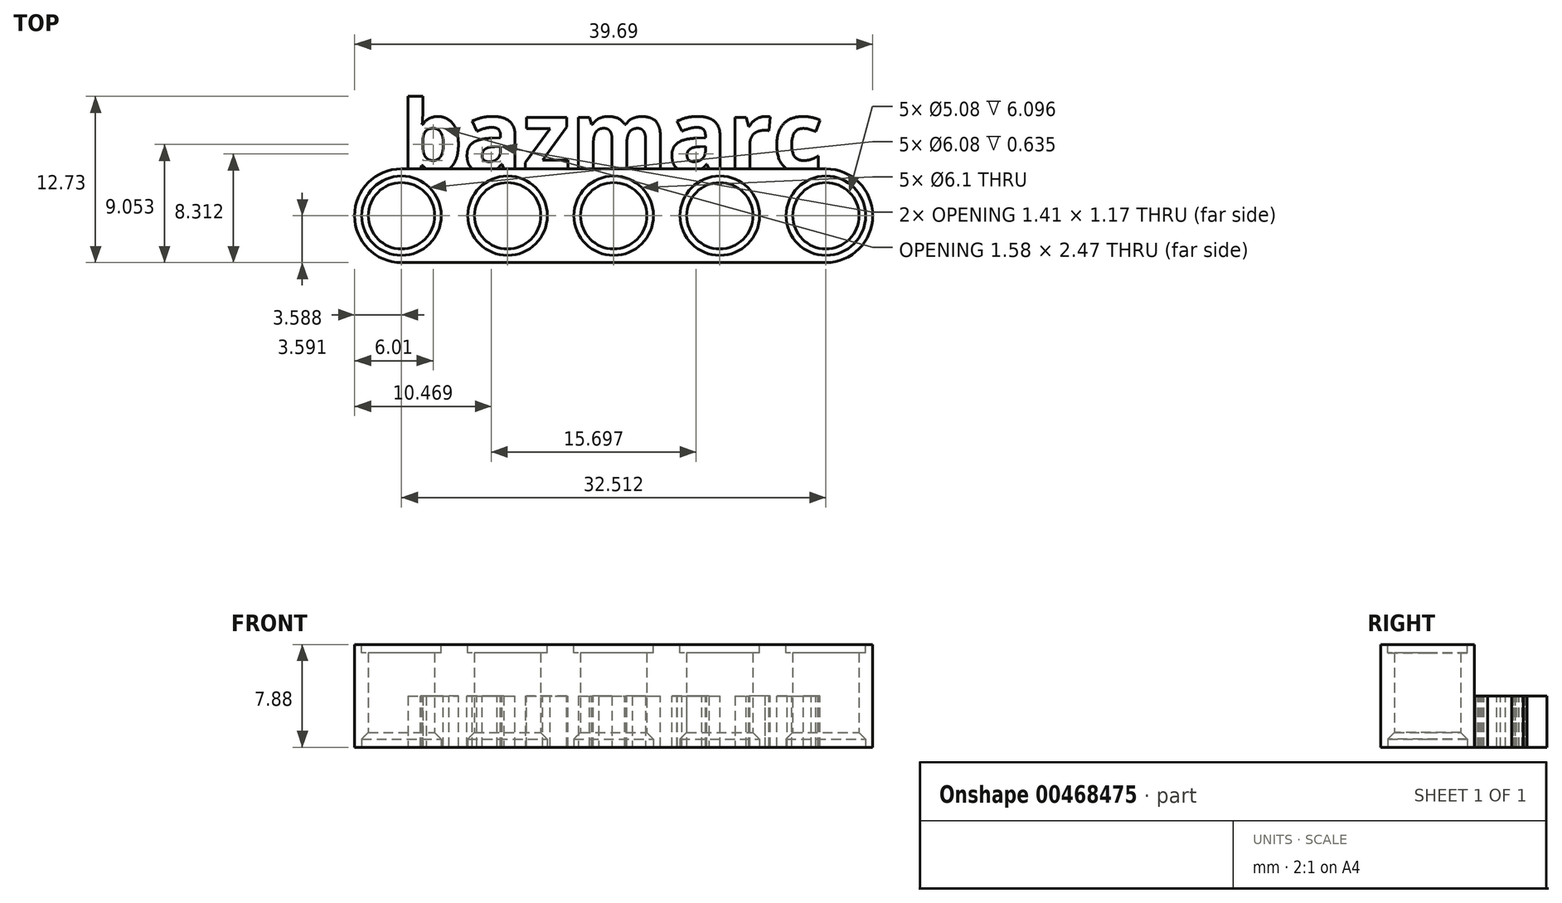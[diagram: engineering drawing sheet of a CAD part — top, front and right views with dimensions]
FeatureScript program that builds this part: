
annotation { "Feature Type Name" : "Feature", "Feature Type Description" : "" }
export const myFeature = defineFeature(function(context is Context, id is Id, definition is map)
    precondition{}
    {
        {
            var Q0;
            Q0=qCreatedBy(makeId("Top.planeOp"),FACE);
            var sketch = newSketch(context, id + "F0", { "sketchPlane" : qUnion([Q0])});
            skCircle(sketch, "E0", {"center": v(-60.84, 14.37) * mm, "radius": 3.6 * mm});
            skCircle(sketch, "E1.1.0.0", {"center": v(-52.71, 14.37) * mm, "radius": 3.6 * mm});
            skCircle(sketch, "E1.2.0.0", {"center": v(-44.59, 14.37) * mm, "radius": 3.6 * mm});
            skCircle(sketch, "E1.3.0.0", {"center": v(-36.46, 14.37) * mm, "radius": 3.6 * mm});
            skLineSegment(sketch, "E1.direction1", {"start": v(-60.84, 14.37) * mm, "end": v(-52.71, 14.37) * mm, "construction": true});
            skCircle(sketch, "E2.0.4.0", {"center": v(-28.33, 14.37) * mm, "radius": 3.6 * mm});
            skLineSegment(sketch, "E3.left", {"start": v(-60.84, 14.37) * mm, "end": v(-60.84, 14.37) * mm});
            skLineSegment(sketch, "E3.right", {"start": v(-28.33, 14.37) * mm, "end": v(-28.33, 14.37) * mm});
            skLineSegment(sketch, "E4.bottom", {"start": v(-60.84, 17.96) * mm, "end": v(-28.33, 17.96) * mm});
            skLineSegment(sketch, "E4.top", {"start": v(-60.84, 10.78) * mm, "end": v(-28.33, 10.78) * mm});
            skCircle(sketch, "E5", {"center": v(-60.84, 14.37) * mm, "radius": 3.05 * mm});
            skCircle(sketch, "E6.1.0.0", {"center": v(-52.71, 14.37) * mm, "radius": 3.05 * mm});
            skCircle(sketch, "E6.2.0.0", {"center": v(-44.59, 14.37) * mm, "radius": 3.05 * mm});
            skCircle(sketch, "E6.3.0.0", {"center": v(-36.46, 14.37) * mm, "radius": 3.05 * mm});
            skCircle(sketch, "E6.4.0.0", {"center": v(-28.33, 14.37) * mm, "radius": 3.05 * mm});
            skCircle(sketch, "E7", {"center": v(-60.84, 14.37) * mm, "radius": 2.54 * mm});
            skCircle(sketch, "E8.1.0.0", {"center": v(-52.71, 14.37) * mm, "radius": 2.54 * mm});
            skCircle(sketch, "E8.2.0.0", {"center": v(-44.59, 14.37) * mm, "radius": 2.54 * mm});
            skCircle(sketch, "E8.3.0.0", {"center": v(-36.46, 14.37) * mm, "radius": 2.54 * mm});
            skCircle(sketch, "E8.4.0.0", {"center": v(-28.33, 14.37) * mm, "radius": 2.54 * mm});
            skSolve(sketch);
        }
        {
            var Q0;
            Q0=makeQuery(id+"F0.imprint","IMPRINT",FACE,{"disambiguationData":[TD([[makeQuery(id+"F0.imprint","IMPRINT",EDGE,{"derivedFrom":sQuery(id+"F0.wireOp",EDGE,"E6.2.0.0")}),1.0]])]});
            var Q1;
            {var subQ0=sQuery(id+"F0.wireOp",EDGE,"E4.bottom");var subQ1=sQuery(id+"F0.wireOp",EDGE,"E0");var subQ2=makeQuery(id+"F0.imprint","INTERSECT",VERTEX,{"derivedFrom":[subQ1,subQ0]});Q1=makeQuery(id+"F0.imprint","IMPRINT",FACE,{"disambiguationData":[TD([[makeQuery(id+"F0.imprint","IMPRINT",EDGE,{"disambiguationData":[TD([[subQ2,1.0]])],"derivedFrom":subQ1}),-1.0]])]});}
            var Q2;
            {var subQ0=sQuery(id+"F0.wireOp",EDGE,"E4.bottom");var subQ1=sQuery(id+"F0.wireOp",EDGE,"E1.1.0.0");var subQ2=makeQuery(id+"F0.imprint","INTERSECT",VERTEX,{"derivedFrom":[subQ1,subQ0]});Q2=makeQuery(id+"F0.imprint","IMPRINT",FACE,{"disambiguationData":[TD([[makeQuery(id+"F0.imprint","IMPRINT",EDGE,{"disambiguationData":[TD([[subQ2,1.0]])],"derivedFrom":subQ1}),-1.0]])]});}
            var Q3;
            Q3=makeQuery(id+"F0.imprint","IMPRINT",FACE,{"disambiguationData":[TD([[makeQuery(id+"F0.imprint","IMPRINT",EDGE,{"derivedFrom":sQuery(id+"F0.wireOp",EDGE,"E6.2.0.0")}),-1.0]])]});
            var Q4;
            Q4=makeQuery(id+"F0.imprint","IMPRINT",FACE,{"disambiguationData":[TD([[makeQuery(id+"F0.imprint","IMPRINT",EDGE,{"derivedFrom":sQuery(id+"F0.wireOp",EDGE,"E6.1.0.0")}),-1.0]])]});
            var Q5;
            Q5=makeQuery(id+"F0.imprint","IMPRINT",FACE,{"disambiguationData":[TD([[makeQuery(id+"F0.imprint","IMPRINT",EDGE,{"derivedFrom":sQuery(id+"F0.wireOp",EDGE,"E6.3.0.0")}),-1.0]])]});
            var Q6;
            Q6=makeQuery(id+"F0.imprint","IMPRINT",FACE,{"disambiguationData":[TD([[makeQuery(id+"F0.imprint","IMPRINT",EDGE,{"derivedFrom":sQuery(id+"F0.wireOp",EDGE,"E6.3.0.0")}),1.0]])]});
            var Q7;
            {var subQ0=sQuery(id+"F0.wireOp",EDGE,"E4.bottom");var subQ1=sQuery(id+"F0.wireOp",EDGE,"E1.3.0.0");var subQ2=makeQuery(id+"F0.imprint","INTERSECT",VERTEX,{"derivedFrom":[subQ1,subQ0]});Q7=makeQuery(id+"F0.imprint","IMPRINT",FACE,{"disambiguationData":[TD([[makeQuery(id+"F0.imprint","IMPRINT",EDGE,{"disambiguationData":[TD([[subQ2,1.0]])],"derivedFrom":subQ1}),-1.0]])]});}
            var Q8;
            Q8=makeQuery(id+"F0.imprint","IMPRINT",FACE,{"disambiguationData":[TD([[makeQuery(id+"F0.imprint","IMPRINT",EDGE,{"derivedFrom":sQuery(id+"F0.wireOp",EDGE,"E6.4.0.0")}),-1.0]])]});
            var Q9;
            Q9=makeQuery(id+"F0.imprint","IMPRINT",FACE,{"disambiguationData":[TD([[makeQuery(id+"F0.imprint","IMPRINT",EDGE,{"derivedFrom":sQuery(id+"F0.wireOp",EDGE,"E6.1.0.0")}),1.0]])]});
            var Q10;
            {var subQ0=sQuery(id+"F0.wireOp",EDGE,"E4.bottom");var subQ1=sQuery(id+"F0.wireOp",EDGE,"E1.2.0.0");var subQ2=makeQuery(id+"F0.imprint","INTERSECT",VERTEX,{"derivedFrom":[subQ1,subQ0]});Q10=makeQuery(id+"F0.imprint","IMPRINT",FACE,{"disambiguationData":[TD([[makeQuery(id+"F0.imprint","IMPRINT",EDGE,{"disambiguationData":[TD([[subQ2,1.0]])],"derivedFrom":subQ1}),-1.0]])]});}
            var Q11;
            Q11=makeQuery(id+"F0.imprint","IMPRINT",FACE,{"disambiguationData":[TD([[makeQuery(id+"F0.imprint","IMPRINT",EDGE,{"derivedFrom":sQuery(id+"F0.wireOp",EDGE,"E6.4.0.0")}),1.0]])]});
            var Q12;
            Q12=makeQuery(id+"F0.imprint","IMPRINT",FACE,{"disambiguationData":[TD([[makeQuery(id+"F0.imprint","IMPRINT",EDGE,{"derivedFrom":sQuery(id+"F0.wireOp",EDGE,"E5")}),-1.0]])]});
            var Q13;
            Q13=makeQuery(id+"F0.imprint","IMPRINT",FACE,{"disambiguationData":[TD([[makeQuery(id+"F0.imprint","IMPRINT",EDGE,{"derivedFrom":sQuery(id+"F0.wireOp",EDGE,"E5")}),1.0]])]});
            extrude(context, id + "F1", {"entities" : qUnion([Q0, Q1, Q2, Q3, Q4, Q5, Q6, Q7, Q8, Q9, Q10, Q11, Q12, Q13]), "endBound" : BoundingType.SYMMETRIC, "depth" : 7.87 * mm});
        }
        {
            var Q0;
            Q0=makeQuery(id+"F1.opExtrude","CAP_FACE",FACE,{"disambiguationData":[OSD([sQuery(id+"F0.wireOp",EDGE,"E0"),sQuery(id+"F0.wireOp",EDGE,"E2.0.4.0"),sQuery(id+"F0.wireOp",EDGE,"E4.bottom"),sQuery(id+"F0.wireOp",EDGE,"E4.top"),sQuery(id+"F0.wireOp",EDGE,"E7"),sQuery(id+"F0.wireOp",EDGE,"E8.1.0.0"),sQuery(id+"F0.wireOp",EDGE,"E8.2.0.0"),sQuery(id+"F0.wireOp",EDGE,"E8.3.0.0"),sQuery(id+"F0.wireOp",EDGE,"E8.4.0.0")])],"isStart":false});
            var sketch = newSketch(context, id + "F2", { "sketchPlane" : qUnion([Q0])});
            skCircle(sketch, "E9", {"center": v(-28.33, 14.37) * mm, "radius": 3.04 * mm});
            skCircle(sketch, "E10.1.0.0", {"center": v(-36.46, 14.37) * mm, "radius": 3.04 * mm});
            skCircle(sketch, "E10.2.0.0", {"center": v(-44.59, 14.37) * mm, "radius": 3.04 * mm});
            skCircle(sketch, "E10.3.0.0", {"center": v(-52.71, 14.37) * mm, "radius": 3.04 * mm});
            skCircle(sketch, "E10.4.0.0", {"center": v(-60.84, 14.37) * mm, "radius": 3.04 * mm});
            skLineSegment(sketch, "E10.direction1", {"start": v(-28.33, 14.37) * mm, "end": v(-36.46, 14.37) * mm, "construction": true});
            skSolve(sketch);
        }
        {
            var Q0;
            Q0 = qSketchRegion(id + "F2", true);
            extrude(context, id + "F3", {"entities" : qUnion([Q0]), "operationType" : NewBodyOperationType.REMOVE, "oppositeDirection" : true, "depth" : 0.64 * mm});
        }
        {
            var Q0;
            Q0=makeQuery(id+"F1.opExtrude","CAP_FACE",FACE,{"disambiguationData":[OSD([sQuery(id+"F0.wireOp",EDGE,"E0"),sQuery(id+"F0.wireOp",EDGE,"E2.0.4.0"),sQuery(id+"F0.wireOp",EDGE,"E4.bottom"),sQuery(id+"F0.wireOp",EDGE,"E4.top"),sQuery(id+"F0.wireOp",EDGE,"E7"),sQuery(id+"F0.wireOp",EDGE,"E8.1.0.0"),sQuery(id+"F0.wireOp",EDGE,"E8.2.0.0"),sQuery(id+"F0.wireOp",EDGE,"E8.3.0.0"),sQuery(id+"F0.wireOp",EDGE,"E8.4.0.0")])],"isStart":true});
            var sketch = newSketch(context, id + "F4", { "sketchPlane" : qUnion([Q0])});
            skCircle(sketch, "E11", {"center": v(-60.84, -14.37) * mm, "radius": 3.05 * mm});
            skCircle(sketch, "E12.1.0.0", {"center": v(-52.71, -14.37) * mm, "radius": 3.05 * mm});
            skCircle(sketch, "E12.2.0.0", {"center": v(-44.59, -14.37) * mm, "radius": 3.05 * mm});
            skCircle(sketch, "E12.3.0.0", {"center": v(-36.46, -14.37) * mm, "radius": 3.05 * mm});
            skCircle(sketch, "E12.4.0.0", {"center": v(-28.33, -14.37) * mm, "radius": 3.05 * mm});
            skLineSegment(sketch, "E12.direction1", {"start": v(-60.84, -14.37) * mm, "end": v(-52.71, -14.37) * mm, "construction": true});
            skSolve(sketch);
        }
        {
            var Q0;
            Q0 = qSketchRegion(id + "F4", true);
            extrude(context, id + "F5", {"entities" : qUnion([Q0]), "operationType" : NewBodyOperationType.REMOVE, "oppositeDirection" : true, "depth" : 0.64 * mm});
        }
        {
            var Q0;
            Q0=qCreatedBy(makeId("Top.planeOp"),FACE);
            var sketch = newSketch(context, id + "F6", { "sketchPlane" : qUnion([Q0])});
            skText(sketch, "E13", { "text": "bazmarc", "fontName": "OpenSans-Bold.ttf"});
            const initialGuessF6  = {"E13": [-0.06093, 0.01776, 1, 0, 0.00545]};
            skSetInitialGuess(sketch, initialGuessF6);
            skSolve(sketch);
        }
        {
            var Q0;
            Q0 = qSketchRegion(id + "F6", true);
            extrude(context, id + "F7", {"entities" : qUnion([Q0]), "operationType" : NewBodyOperationType.ADD, "oppositeDirection" : true, "depth" : 3.94 * mm});
        }
        {
            var Q0;
            Q0=makeQuery(id+"F5.boolean.opBoolean","INTERSECT",EDGE,{"derivedFrom":[makeQuery(id+"F1.opExtrude","SWEPT_FACE",FACE,{"disambiguationData":[OSD([sQuery(id+"F0.wireOp",EDGE,"E8.3.0.0")])]}),makeQuery(id+"F5.opExtrude","CAP_FACE",FACE,{"disambiguationData":[OSD([sQuery(id+"F4.wireOp",EDGE,"E12.3.0.0")])],"isStart":false})]});
            chamfer(context, id + "F8", {"entities" : qUnion([Q0]), "chamferType" : ChamferType.OFFSET_ANGLE, "width" : 0.5 * mm, "oppositeDirection" : false, "angle" : 45 * degree});
        }
        {
            var Q0;
            Q0=makeQuery(id+"F5.boolean.opBoolean","INTERSECT",EDGE,{"derivedFrom":[makeQuery(id+"F1.opExtrude","SWEPT_FACE",FACE,{"disambiguationData":[OSD([sQuery(id+"F0.wireOp",EDGE,"E8.2.0.0")])]}),makeQuery(id+"F5.opExtrude","CAP_FACE",FACE,{"disambiguationData":[OSD([sQuery(id+"F4.wireOp",EDGE,"E12.2.0.0")])],"isStart":false})]});
            var Q1;
            Q1=makeQuery(id+"F5.boolean.opBoolean","INTERSECT",EDGE,{"derivedFrom":[makeQuery(id+"F1.opExtrude","SWEPT_FACE",FACE,{"disambiguationData":[OSD([sQuery(id+"F0.wireOp",EDGE,"E8.1.0.0")])]}),makeQuery(id+"F5.opExtrude","CAP_FACE",FACE,{"disambiguationData":[OSD([sQuery(id+"F4.wireOp",EDGE,"E12.1.0.0")])],"isStart":false})]});
            var Q2;
            Q2=makeQuery(id+"F5.boolean.opBoolean","INTERSECT",EDGE,{"derivedFrom":[makeQuery(id+"F1.opExtrude","SWEPT_FACE",FACE,{"disambiguationData":[OSD([sQuery(id+"F0.wireOp",EDGE,"E7")])]}),makeQuery(id+"F5.opExtrude","CAP_FACE",FACE,{"disambiguationData":[OSD([sQuery(id+"F4.wireOp",EDGE,"E11")])],"isStart":false})]});
            var Q3;
            Q3=makeQuery(id+"F5.boolean.opBoolean","INTERSECT",EDGE,{"derivedFrom":[makeQuery(id+"F1.opExtrude","SWEPT_FACE",FACE,{"disambiguationData":[OSD([sQuery(id+"F0.wireOp",EDGE,"E8.4.0.0")])]}),makeQuery(id+"F5.opExtrude","CAP_FACE",FACE,{"disambiguationData":[OSD([sQuery(id+"F4.wireOp",EDGE,"E12.4.0.0")])],"isStart":false})]});
            chamfer(context, id + "F9", {"entities" : qUnion([Q0, Q1, Q2, Q3]), "chamferType" : ChamferType.OFFSET_ANGLE, "width" : 0.5 * mm, "oppositeDirection" : false, "angle" : 45 * degree});
        }
    });
